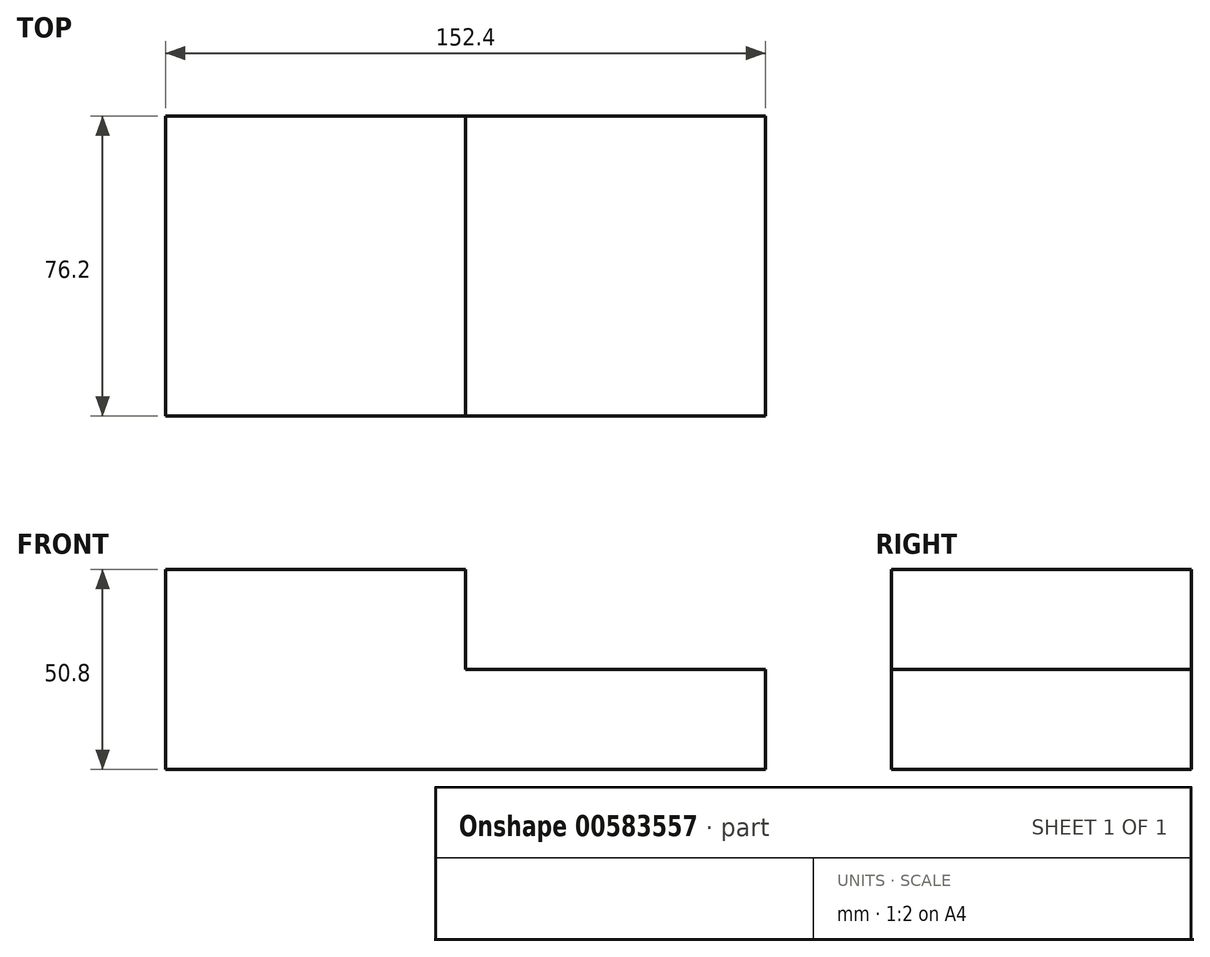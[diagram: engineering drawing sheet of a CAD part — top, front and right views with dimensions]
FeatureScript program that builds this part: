
annotation { "Feature Type Name" : "Feature", "Feature Type Description" : "" }
export const myFeature = defineFeature(function(context is Context, id is Id, definition is map)
    precondition{}
    {
        {
            var Q0;
            Q0=qCreatedBy(makeId("Front.planeOp"),FACE);
            var sketch = newSketch(context, id + "F0", { "sketchPlane" : qUnion([Q0])});
            skLineSegment(sketch, "E0", {"start": v(0, 0) * mm, "end": v(152.4, 0) * mm});
            skLineSegment(sketch, "E1", {"start": v(143.12, -41.71) * mm, "end": v(123.9, -47.6) * mm});
            skLineSegment(sketch, "E2", {"start": v(0, 0) * mm, "end": v(0, 50.8) * mm});
            skLineSegment(sketch, "E3", {"start": v(0, 50.8) * mm, "end": v(76.2, 50.8) * mm});
            skLineSegment(sketch, "E4", {"start": v(76.2, 50.8) * mm, "end": v(76.2, 25.4) * mm});
            skLineSegment(sketch, "E5", {"start": v(76.2, 25.4) * mm, "end": v(152.4, 25.4) * mm});
            skLineSegment(sketch, "E6", {"start": v(152.4, 25.4) * mm, "end": v(152.4, 0) * mm});
            skSolve(sketch);
        }
        {
            var Q0;
            Q0 = qSketchRegion(id + "F0", true);
            extrude(context, id + "F1", {"entities" : qUnion([Q0]), "depth" : 76.2 * mm, "offsetDistance" : 25.4 * mm});
        }
    });
